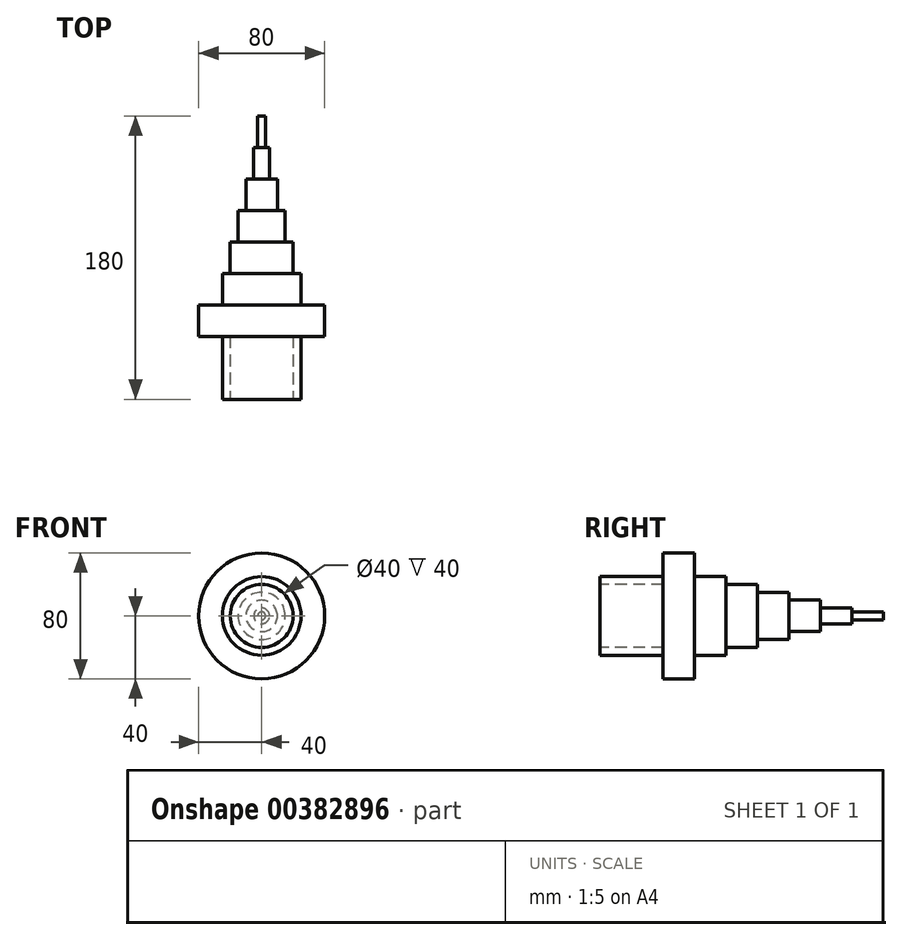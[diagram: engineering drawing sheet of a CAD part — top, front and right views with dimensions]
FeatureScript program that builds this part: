
annotation { "Feature Type Name" : "Feature", "Feature Type Description" : "" }
export const myFeature = defineFeature(function(context is Context, id is Id, definition is map)
    precondition{}
    {
        {
            var Q0;
            Q0=qCreatedBy(makeId("Right.planeOp"),FACE);
            var sketch = newSketch(context, id + "F0", { "sketchPlane" : qUnion([Q0])});
            skLineSegment(sketch, "E0", {"start": v(-100, 0) * mm, "end": v(80, 0) * mm, "construction": true});
            skLineSegment(sketch, "E1.bottom", {"start": v(-100, 0) * mm, "end": v(-60, 0) * mm});
            skLineSegment(sketch, "E1.top", {"start": v(-100, 25) * mm, "end": v(-60, 25) * mm});
            skLineSegment(sketch, "E1.left", {"start": v(-100, 0) * mm, "end": v(-100, 25) * mm});
            skLineSegment(sketch, "E1.right", {"start": v(-60, 0) * mm, "end": v(-60, 25) * mm});
            skLineSegment(sketch, "E2.bottom", {"start": v(-60, 0) * mm, "end": v(-40, 0) * mm});
            skLineSegment(sketch, "E2.top", {"start": v(-60, 40) * mm, "end": v(-40, 40) * mm});
            skLineSegment(sketch, "E2.left", {"start": v(-60, 0) * mm, "end": v(-60, 40) * mm});
            skLineSegment(sketch, "E2.right", {"start": v(-40, 0) * mm, "end": v(-40, 40) * mm});
            skLineSegment(sketch, "E3.bottom", {"start": v(-40, 0) * mm, "end": v(-20, 0) * mm});
            skLineSegment(sketch, "E3.top", {"start": v(-40, 25) * mm, "end": v(-20, 25) * mm});
            skLineSegment(sketch, "E3.left", {"start": v(-40, 0) * mm, "end": v(-40, 25) * mm});
            skLineSegment(sketch, "E3.right", {"start": v(-20, 0) * mm, "end": v(-20, 25) * mm});
            skLineSegment(sketch, "E4.bottom", {"start": v(-20, 0) * mm, "end": v(0, 0) * mm});
            skLineSegment(sketch, "E4.top", {"start": v(-20, 20) * mm, "end": v(0, 20) * mm});
            skLineSegment(sketch, "E4.left", {"start": v(-20, 0) * mm, "end": v(-20, 20) * mm});
            skLineSegment(sketch, "E4.right", {"start": v(0, 0) * mm, "end": v(0, 20) * mm});
            skLineSegment(sketch, "E5.bottom", {"start": v(0, 0) * mm, "end": v(20, 0) * mm});
            skLineSegment(sketch, "E5.top", {"start": v(0, 15) * mm, "end": v(20, 15) * mm});
            skLineSegment(sketch, "E5.left", {"start": v(0, 0) * mm, "end": v(0, 15) * mm});
            skLineSegment(sketch, "E5.right", {"start": v(20, 0) * mm, "end": v(20, 15) * mm});
            skLineSegment(sketch, "E6.bottom", {"start": v(20, 0) * mm, "end": v(40, 0) * mm});
            skLineSegment(sketch, "E6.top", {"start": v(20, 10) * mm, "end": v(40, 10) * mm});
            skLineSegment(sketch, "E6.left", {"start": v(20, 0) * mm, "end": v(20, 10) * mm});
            skLineSegment(sketch, "E6.right", {"start": v(40, 0) * mm, "end": v(40, 10) * mm});
            skLineSegment(sketch, "E7.bottom", {"start": v(40, 0) * mm, "end": v(60, 0) * mm});
            skLineSegment(sketch, "E7.top", {"start": v(40, 5) * mm, "end": v(60, 5) * mm});
            skLineSegment(sketch, "E7.left", {"start": v(40, 0) * mm, "end": v(40, 5) * mm});
            skLineSegment(sketch, "E7.right", {"start": v(60, 0) * mm, "end": v(60, 5) * mm});
            skLineSegment(sketch, "E8.bottom", {"start": v(60, 0) * mm, "end": v(80, 0) * mm});
            skLineSegment(sketch, "E8.top", {"start": v(60, 2.5) * mm, "end": v(80, 2.5) * mm});
            skLineSegment(sketch, "E8.left", {"start": v(60, 0) * mm, "end": v(60, 2.5) * mm});
            skLineSegment(sketch, "E8.right", {"start": v(80, 0) * mm, "end": v(80, 2.5) * mm});
            skLineSegment(sketch, "E9", {"start": v(-100, 20) * mm, "end": v(-60, 20) * mm});
            skSolve(sketch);
        }
        {
            var Q0;
            {var subQ0=sQuery(id+"F0.wireOp",EDGE,"E1.top");Q0=makeQuery(id+"F0.imprint","IMPRINT",FACE,{"disambiguationData":[TD([[makeQuery(id+"F0.imprint","IMPRINT",EDGE,{"derivedFrom":subQ0}),-1.0]])]});}
            var Q1;
            {var subQ3=sQuery(id+"F0.wireOp",EDGE,"E2.bottom");Q1=makeQuery(id+"F0.imprint","IMPRINT",FACE,{"disambiguationData":[TD([[makeQuery(id+"F0.imprint","IMPRINT",EDGE,{"derivedFrom":subQ3}),1.0]])]});}
            var Q2;
            Q2=makeQuery(id+"F0.imprint","IMPRINT",FACE,{"disambiguationData":[TD([[makeQuery(id+"F0.imprint","IMPRINT",EDGE,{"derivedFrom":sQuery(id+"F0.wireOp",EDGE,"E3.bottom")}),1.0]])]});
            var Q3;
            Q3=makeQuery(id+"F0.imprint","IMPRINT",FACE,{"disambiguationData":[TD([[makeQuery(id+"F0.imprint","IMPRINT",EDGE,{"derivedFrom":sQuery(id+"F0.wireOp",EDGE,"E4.bottom")}),1.0]])]});
            var Q4;
            Q4=makeQuery(id+"F0.imprint","IMPRINT",FACE,{"disambiguationData":[TD([[makeQuery(id+"F0.imprint","IMPRINT",EDGE,{"derivedFrom":sQuery(id+"F0.wireOp",EDGE,"E5.bottom")}),1.0]])]});
            var Q5;
            Q5=makeQuery(id+"F0.imprint","IMPRINT",FACE,{"disambiguationData":[TD([[makeQuery(id+"F0.imprint","IMPRINT",EDGE,{"derivedFrom":sQuery(id+"F0.wireOp",EDGE,"E6.bottom")}),1.0]])]});
            var Q6;
            Q6=makeQuery(id+"F0.imprint","IMPRINT",FACE,{"disambiguationData":[TD([[makeQuery(id+"F0.imprint","IMPRINT",EDGE,{"derivedFrom":sQuery(id+"F0.wireOp",EDGE,"E7.bottom")}),1.0]])]});
            var Q7;
            Q7=makeQuery(id+"F0.imprint","IMPRINT",FACE,{"disambiguationData":[TD([[makeQuery(id+"F0.imprint","IMPRINT",EDGE,{"derivedFrom":sQuery(id+"F0.wireOp",EDGE,"E8.bottom")}),1.0]])]});
            var Q8;
            Q8=sQuery(id+"F0.wireOp",EDGE,"E3.bottom");
            revolve(context, id + "F1", {"entities" : qUnion([Q0, Q1, Q2, Q3, Q4, Q5, Q6, Q7]), "axis" : qUnion([Q8]), "revolveType" : RevolveType.FULL});
        }
    });
